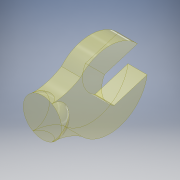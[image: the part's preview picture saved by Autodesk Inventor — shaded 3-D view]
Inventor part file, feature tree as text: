
AUTODESK INVENTOR PART (.ipt)
format: ipt  version: 2017 (Build 210142000, 142)  size: 134,656 bytes
history: native  units: mm
features: sketch x2, revolve x1, extrude x1
ambient origin geometry x8: Origin, YZ Plane, XZ Plane, XY Plane, X Axis, Y Axis, Z Axis, Center Point
bodies: Solid1 (feature_tree)
feature tree (4):
  revolve  "Revolution1"  [1 undecoded]
  extrude  "Extrusion1"  Depth=23.0mm
  sketch  "Sketch1"  dims[d1=180.0deg d2=7.5mm]
  sketch  "Sketch2"  dims[d11=23.0mm d15=23.0mm d16=23.0mm d17=7.5mm d18=0.0mm]
note: 1 required parameter value undecoded (feature->parameter linkage not recoverable at this tier; creation-order binding heuristic only, values carry confidence <= 0.55)
